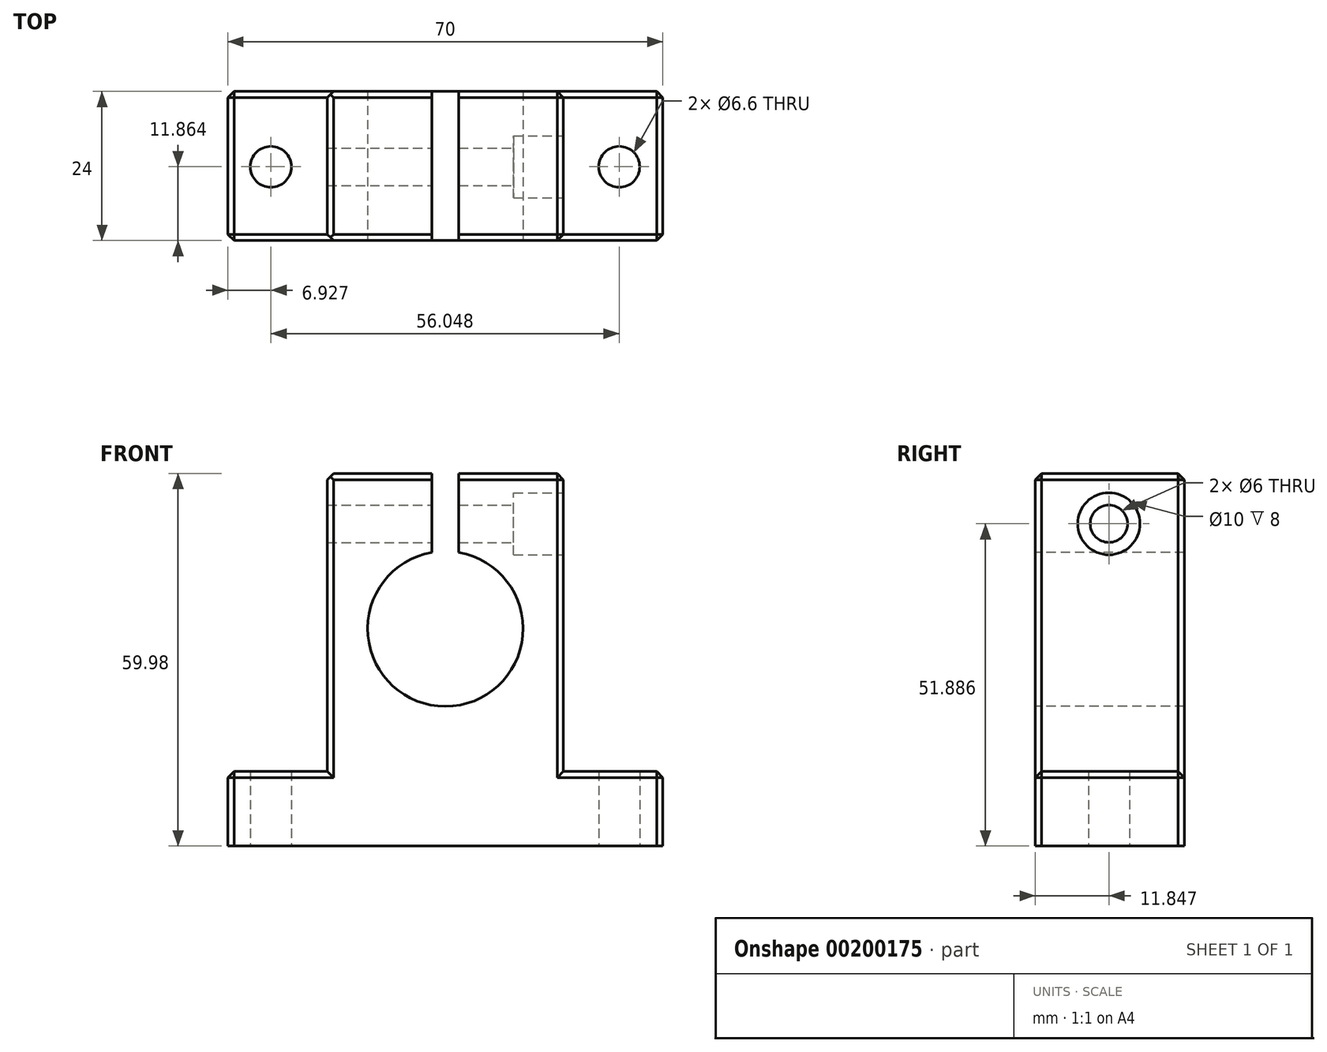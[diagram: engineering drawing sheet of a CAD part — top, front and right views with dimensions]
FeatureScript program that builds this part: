
annotation { "Feature Type Name" : "Feature", "Feature Type Description" : "" }
export const myFeature = defineFeature(function(context is Context, id is Id, definition is map)
    precondition{}
    {
        {
            var Q0;
            Q0=qCreatedBy(makeId("Front.planeOp"),FACE);
            var sketch = newSketch(context, id + "F0", { "sketchPlane" : qUnion([Q0])});
            skLineSegment(sketch, "E0", {"start": v(-119.4, -35) * mm, "end": v(145.74, -35) * mm});
            skSolve(sketch);
        }
        {
            var Q0;
            Q0=qCreatedBy(makeId("Front.planeOp"),FACE);
            var sketch = newSketch(context, id + "F1", { "sketchPlane" : qUnion([Q0])});
            skLineSegment(sketch, "E1.bottom", {"start": v(-35, -22.98) * mm, "end": v(35, -22.98) * mm});
            skLineSegment(sketch, "E1.top", {"start": v(-35, -34.98) * mm, "end": v(35, -34.98) * mm});
            skLineSegment(sketch, "E1.left", {"start": v(-35, -22.98) * mm, "end": v(-35, -34.98) * mm});
            skLineSegment(sketch, "E1.right", {"start": v(35, -22.98) * mm, "end": v(35, -34.98) * mm});
            skPoint(sketch, "E1.middle", {"position": v(0, -28.98) * mm});
            skSolve(sketch);
        }
        {
            var Q0;
            Q0 = qSketchRegion(id + "F1", true);
            extrude(context, id + "F2", {"entities" : qUnion([Q0]), "depth" : 24 * mm});
        }
        {
            var Q0;
            Q0=qCreatedBy(makeId("Front.planeOp"),FACE);
            var sketch = newSketch(context, id + "F3", { "sketchPlane" : qUnion([Q0])});
            skLineSegment(sketch, "E2.bottom", {"start": v(-19, 25) * mm, "end": v(19, 25) * mm});
            skLineSegment(sketch, "E2.top", {"start": v(-19, -25) * mm, "end": v(19, -25) * mm});
            skLineSegment(sketch, "E2.left", {"start": v(-19, 25) * mm, "end": v(-19, -25) * mm});
            skLineSegment(sketch, "E2.right", {"start": v(19, 25) * mm, "end": v(19, -25) * mm});
            skPoint(sketch, "E2.middle", {"position": v(0, 0) * mm});
            skSolve(sketch);
        }
        {
            var Q0;
            Q0=makeQuery(id+"F3.imprint","IMPRINT",FACE,{"disambiguationData":[TD([[makeQuery(id+"F3.imprint","IMPRINT",EDGE,{"derivedFrom":sQuery(id+"F3.wireOp",EDGE,"E2.bottom")}),-1.0]])]});
            extrude(context, id + "F4", {"entities" : qUnion([Q0]), "operationType" : NewBodyOperationType.ADD, "depth" : 24 * mm});
        }
        {
            var Q0;
            Q0=makeQuery(id+"F4.boolean.opBoolean","MERGE",FACE,{"derivedFrom":[makeQuery(id+"F2.opExtrude","CAP_FACE",FACE,{"disambiguationData":[OSD([sQuery(id+"F1.wireOp",EDGE,"E1.bottom"),sQuery(id+"F1.wireOp",EDGE,"E1.top"),sQuery(id+"F1.wireOp",EDGE,"E1.left"),sQuery(id+"F1.wireOp",EDGE,"E1.right")])],"isStart":false}),makeQuery(id+"F4.opExtrude","CAP_FACE",FACE,{"disambiguationData":[OSD([sQuery(id+"F3.wireOp",EDGE,"E2.bottom"),sQuery(id+"F3.wireOp",EDGE,"E2.top"),sQuery(id+"F3.wireOp",EDGE,"E2.left"),sQuery(id+"F3.wireOp",EDGE,"E2.right")])],"isStart":false})]});
            var sketch = newSketch(context, id + "F5", { "sketchPlane" : qUnion([Q0])});
            skCircle(sketch, "E3", {"center": v(0, 0) * mm, "radius": 12.5 * mm});
            skSolve(sketch);
        }
        {
            var Q0;
            Q0=makeQuery(id+"F5.imprint","IMPRINT",FACE,{"disambiguationData":[TD([[makeQuery(id+"F5.imprint","IMPRINT",EDGE,{"derivedFrom":sQuery(id+"F5.wireOp",EDGE,"E3")}),1.0]])]});
            extrude(context, id + "F6", {"entities" : qUnion([Q0]), "operationType" : NewBodyOperationType.REMOVE, "oppositeDirection" : true, "depth" : 24 * mm});
        }
        {
            var Q0;
            Q0=qCreatedBy(makeId("Front.planeOp"),FACE);
            var sketch = newSketch(context, id + "F7", { "sketchPlane" : qUnion([Q0])});
            skLineSegment(sketch, "E4.bottom", {"start": v(-2.17, 28.75) * mm, "end": v(2.17, 28.75) * mm});
            skLineSegment(sketch, "E4.top", {"start": v(-2.17, 9.9) * mm, "end": v(2.17, 9.9) * mm});
            skLineSegment(sketch, "E4.left", {"start": v(-2.17, 28.75) * mm, "end": v(-2.17, 9.9) * mm});
            skLineSegment(sketch, "E4.right", {"start": v(2.17, 28.75) * mm, "end": v(2.17, 9.9) * mm});
            skPoint(sketch, "E4.middle", {"position": v(0, 19.33) * mm});
            skSolve(sketch);
        }
        {
            var Q0;
            Q0=makeQuery(id+"F7.imprint","IMPRINT",FACE,{"disambiguationData":[TD([[makeQuery(id+"F7.imprint","IMPRINT",EDGE,{"derivedFrom":sQuery(id+"F7.wireOp",EDGE,"E4.bottom")}),-1.0]])]});
            extrude(context, id + "F8", {"entities" : qUnion([Q0]), "operationType" : NewBodyOperationType.REMOVE, "depth" : 24 * mm});
        }
        {
            var Q0;
            Q0=makeQuery(id+"F2.opExtrude","SWEPT_FACE",FACE,{"disambiguationData":[OSD([sQuery(id+"F1.wireOp",EDGE,"E1.top")])]});
            var sketch = newSketch(context, id + "F9", { "sketchPlane" : qUnion([Q0])});
            skCircle(sketch, "E5", {"center": v(-28.07, 12.14) * mm, "radius": 3.3 * mm});
            skSolve(sketch);
        }
        {
            var Q0;
            Q0=makeQuery(id+"F9.imprint","IMPRINT",FACE,{"disambiguationData":[TD([[makeQuery(id+"F9.imprint","IMPRINT",EDGE,{"derivedFrom":sQuery(id+"F9.wireOp",EDGE,"E5")}),1.0]])]});
            extrude(context, id + "F10", {"entities" : qUnion([Q0]), "operationType" : NewBodyOperationType.REMOVE, "oppositeDirection" : true, "depth" : 25 * mm});
        }
        {
            var Q0;
            Q0=makeQuery(id+"F2.opExtrude","SWEPT_FACE",FACE,{"disambiguationData":[OSD([sQuery(id+"F1.wireOp",EDGE,"E1.top")])]});
            var sketch = newSketch(context, id + "F11", { "sketchPlane" : qUnion([Q0])});
            skCircle(sketch, "E6", {"center": v(27.98, 12.14) * mm, "radius": 3.3 * mm});
            skSolve(sketch);
        }
        {
            var Q0;
            Q0=makeQuery(id+"F11.imprint","IMPRINT",FACE,{"disambiguationData":[TD([[makeQuery(id+"F11.imprint","IMPRINT",EDGE,{"derivedFrom":sQuery(id+"F11.wireOp",EDGE,"E6")}),1.0]])]});
            extrude(context, id + "F12", {"entities" : qUnion([Q0]), "operationType" : NewBodyOperationType.REMOVE, "oppositeDirection" : true, "depth" : 25 * mm});
        }
        {
            var Q0;
            Q0=makeQuery(id+"F4.opExtrude","SWEPT_FACE",FACE,{"disambiguationData":[OSD([sQuery(id+"F3.wireOp",EDGE,"E2.right")])]});
            var sketch = newSketch(context, id + "F13", { "sketchPlane" : qUnion([Q0])});
            skCircle(sketch, "E7", {"center": v(-12.15, 16.9) * mm, "radius": 3 * mm});
            skSolve(sketch);
        }
        {
            var Q0;
            Q0=makeQuery(id+"F13.imprint","IMPRINT",FACE,{"disambiguationData":[TD([[makeQuery(id+"F13.imprint","IMPRINT",EDGE,{"derivedFrom":sQuery(id+"F13.wireOp",EDGE,"E7")}),1.0]])]});
            extrude(context, id + "F14", {"entities" : qUnion([Q0]), "operationType" : NewBodyOperationType.REMOVE, "oppositeDirection" : true, "depth" : 50 * mm});
        }
        {
            var Q0;
            Q0=makeQuery(id+"F4.opExtrude","SWEPT_FACE",FACE,{"disambiguationData":[OSD([sQuery(id+"F3.wireOp",EDGE,"E2.right")])]});
            var sketch = newSketch(context, id + "F15", { "sketchPlane" : qUnion([Q0])});
            skCircle(sketch, "E8", {"center": v(-12.15, 16.9) * mm, "radius": 5 * mm});
            skSolve(sketch);
        }
        {
            var Q0;
            Q0=makeQuery(id+"F15.imprint","IMPRINT",FACE,{"disambiguationData":[TD([[makeQuery(id+"F15.imprint","IMPRINT",EDGE,{"derivedFrom":sQuery(id+"F15.wireOp",EDGE,"E8")}),1.0]])]});
            extrude(context, id + "F16", {"entities" : qUnion([Q0]), "operationType" : NewBodyOperationType.REMOVE, "oppositeDirection" : true, "depth" : 8 * mm});
        }
        {
            var Q0;
            Q0=makeQuery(id+"F4.opExtrude","CAP_EDGE",EDGE,{"disambiguationData":[OSD([sQuery(id+"F3.wireOp",EDGE,"E2.right")])],"isStart":true});
            var Q1;
            Q1=makeQuery(id+"F4.opExtrude","SWEPT_EDGE",EDGE,{"disambiguationData":[OSD([sQuery(id+"F3.wireOp",EDGE,"E2.bottom"),sQuery(id+"F3.wireOp",EDGE,"E2.right")])]});
            var Q2;
            Q2=makeQuery(id+"F4.opExtrude","CAP_EDGE",EDGE,{"disambiguationData":[OSD([sQuery(id+"F3.wireOp",EDGE,"E2.right")])],"isStart":false});
            var Q3;
            {var subQ1=sQuery(id+"F1.wireOp",EDGE,"E1.right");var subQ2=sQuery(id+"F1.wireOp",EDGE,"E1.bottom");Q3=makeQuery(id+"F4.boolean.opBoolean","SPLIT",EDGE,{"disambiguationData":[TD([makeQuery(id+"F2.opExtrude","SWEPT_FACE",FACE,{"disambiguationData":[OSD([subQ1])]})])],"derivedFrom":makeQuery(id+"F2.opExtrude","CAP_EDGE",EDGE,{"disambiguationData":[OSD([subQ2])],"isStart":true})});}
            var Q4;
            Q4=makeQuery(id+"F2.opExtrude","SWEPT_EDGE",EDGE,{"disambiguationData":[OSD([sQuery(id+"F1.wireOp",EDGE,"E1.bottom"),sQuery(id+"F1.wireOp",EDGE,"E1.right")])]});
            var Q5;
            {var subQ1=sQuery(id+"F1.wireOp",EDGE,"E1.right");var subQ2=sQuery(id+"F1.wireOp",EDGE,"E1.bottom");Q5=makeQuery(id+"F4.boolean.opBoolean","SPLIT",EDGE,{"disambiguationData":[TD([makeQuery(id+"F2.opExtrude","SWEPT_FACE",FACE,{"disambiguationData":[OSD([subQ1])]})])],"derivedFrom":makeQuery(id+"F2.opExtrude","CAP_EDGE",EDGE,{"disambiguationData":[OSD([subQ2])],"isStart":false})});}
            var Q6;
            Q6=makeQuery(id+"F2.opExtrude","CAP_EDGE",EDGE,{"disambiguationData":[OSD([sQuery(id+"F1.wireOp",EDGE,"E1.right")])],"isStart":true});
            var Q7;
            Q7=makeQuery(id+"F2.opExtrude","CAP_EDGE",EDGE,{"disambiguationData":[OSD([sQuery(id+"F1.wireOp",EDGE,"E1.right")])],"isStart":false});
            var Q8;
            {var subQ0=sQuery(id+"F3.wireOp",EDGE,"E2.right");var subQ1=sQuery(id+"F3.wireOp",EDGE,"E2.bottom");Q8=makeQuery(id+"F8.boolean.opBoolean","SPLIT",EDGE,{"disambiguationData":[TD([makeQuery(id+"F4.opExtrude","SWEPT_FACE",FACE,{"disambiguationData":[OSD([subQ0])]})])],"derivedFrom":makeQuery(id+"F4.opExtrude","CAP_EDGE",EDGE,{"disambiguationData":[OSD([subQ1])],"isStart":false})});}
            var Q9;
            {var subQ0=sQuery(id+"F3.wireOp",EDGE,"E2.left");var subQ1=sQuery(id+"F3.wireOp",EDGE,"E2.bottom");Q9=makeQuery(id+"F8.boolean.opBoolean","SPLIT",EDGE,{"disambiguationData":[TD([makeQuery(id+"F4.opExtrude","SWEPT_FACE",FACE,{"disambiguationData":[OSD([subQ0])]})])],"derivedFrom":makeQuery(id+"F4.opExtrude","CAP_EDGE",EDGE,{"disambiguationData":[OSD([subQ1])],"isStart":false})});}
            var Q10;
            {var subQ0=sQuery(id+"F3.wireOp",EDGE,"E2.left");var subQ1=sQuery(id+"F3.wireOp",EDGE,"E2.bottom");Q10=makeQuery(id+"F8.boolean.opBoolean","SPLIT",EDGE,{"disambiguationData":[TD([makeQuery(id+"F4.opExtrude","SWEPT_FACE",FACE,{"disambiguationData":[OSD([subQ0])]})])],"derivedFrom":makeQuery(id+"F4.opExtrude","CAP_EDGE",EDGE,{"disambiguationData":[OSD([subQ1])],"isStart":true})});}
            var Q11;
            {var subQ0=sQuery(id+"F3.wireOp",EDGE,"E2.right");var subQ1=sQuery(id+"F3.wireOp",EDGE,"E2.bottom");Q11=makeQuery(id+"F8.boolean.opBoolean","SPLIT",EDGE,{"disambiguationData":[TD([makeQuery(id+"F4.opExtrude","SWEPT_FACE",FACE,{"disambiguationData":[OSD([subQ0])]})])],"derivedFrom":makeQuery(id+"F4.opExtrude","CAP_EDGE",EDGE,{"disambiguationData":[OSD([subQ1])],"isStart":true})});}
            chamfer(context, id + "F17", {"entities" : qUnion([Q0, Q1, Q2, Q3, Q4, Q5, Q6, Q7, Q8, Q9, Q10, Q11]), "width" : 1 * mm, "tangentPropagation" : true});
        }
        {
            var Q0;
            Q0=makeQuery(id+"F4.opExtrude","SWEPT_EDGE",EDGE,{"disambiguationData":[OSD([sQuery(id+"F3.wireOp",EDGE,"E2.bottom"),sQuery(id+"F3.wireOp",EDGE,"E2.left")])]});
            var Q1;
            Q1=makeQuery(id+"F4.opExtrude","CAP_EDGE",EDGE,{"disambiguationData":[OSD([sQuery(id+"F3.wireOp",EDGE,"E2.left")])],"isStart":true});
            var Q2;
            Q2=makeQuery(id+"F4.opExtrude","CAP_EDGE",EDGE,{"disambiguationData":[OSD([sQuery(id+"F3.wireOp",EDGE,"E2.left")])],"isStart":false});
            var Q3;
            {var subQ1=sQuery(id+"F1.wireOp",EDGE,"E1.left");var subQ2=sQuery(id+"F1.wireOp",EDGE,"E1.bottom");Q3=makeQuery(id+"F4.boolean.opBoolean","SPLIT",EDGE,{"disambiguationData":[TD([makeQuery(id+"F2.opExtrude","SWEPT_FACE",FACE,{"disambiguationData":[OSD([subQ1])]})])],"derivedFrom":makeQuery(id+"F2.opExtrude","CAP_EDGE",EDGE,{"disambiguationData":[OSD([subQ2])],"isStart":false})});}
            var Q4;
            Q4=makeQuery(id+"F2.opExtrude","SWEPT_EDGE",EDGE,{"disambiguationData":[OSD([sQuery(id+"F1.wireOp",EDGE,"E1.bottom"),sQuery(id+"F1.wireOp",EDGE,"E1.left")])]});
            var Q5;
            {var subQ1=sQuery(id+"F1.wireOp",EDGE,"E1.left");var subQ2=sQuery(id+"F1.wireOp",EDGE,"E1.bottom");Q5=makeQuery(id+"F4.boolean.opBoolean","SPLIT",EDGE,{"disambiguationData":[TD([makeQuery(id+"F2.opExtrude","SWEPT_FACE",FACE,{"disambiguationData":[OSD([subQ1])]})])],"derivedFrom":makeQuery(id+"F2.opExtrude","CAP_EDGE",EDGE,{"disambiguationData":[OSD([subQ2])],"isStart":true})});}
            var Q6;
            Q6=makeQuery(id+"F2.opExtrude","CAP_EDGE",EDGE,{"disambiguationData":[OSD([sQuery(id+"F1.wireOp",EDGE,"E1.left")])],"isStart":true});
            var Q7;
            Q7=makeQuery(id+"F2.opExtrude","CAP_EDGE",EDGE,{"disambiguationData":[OSD([sQuery(id+"F1.wireOp",EDGE,"E1.left")])],"isStart":false});
            chamfer(context, id + "F18", {"entities" : qUnion([Q0, Q1, Q2, Q3, Q4, Q5, Q6, Q7]), "width" : 1 * mm, "tangentPropagation" : true});
        }
    });
